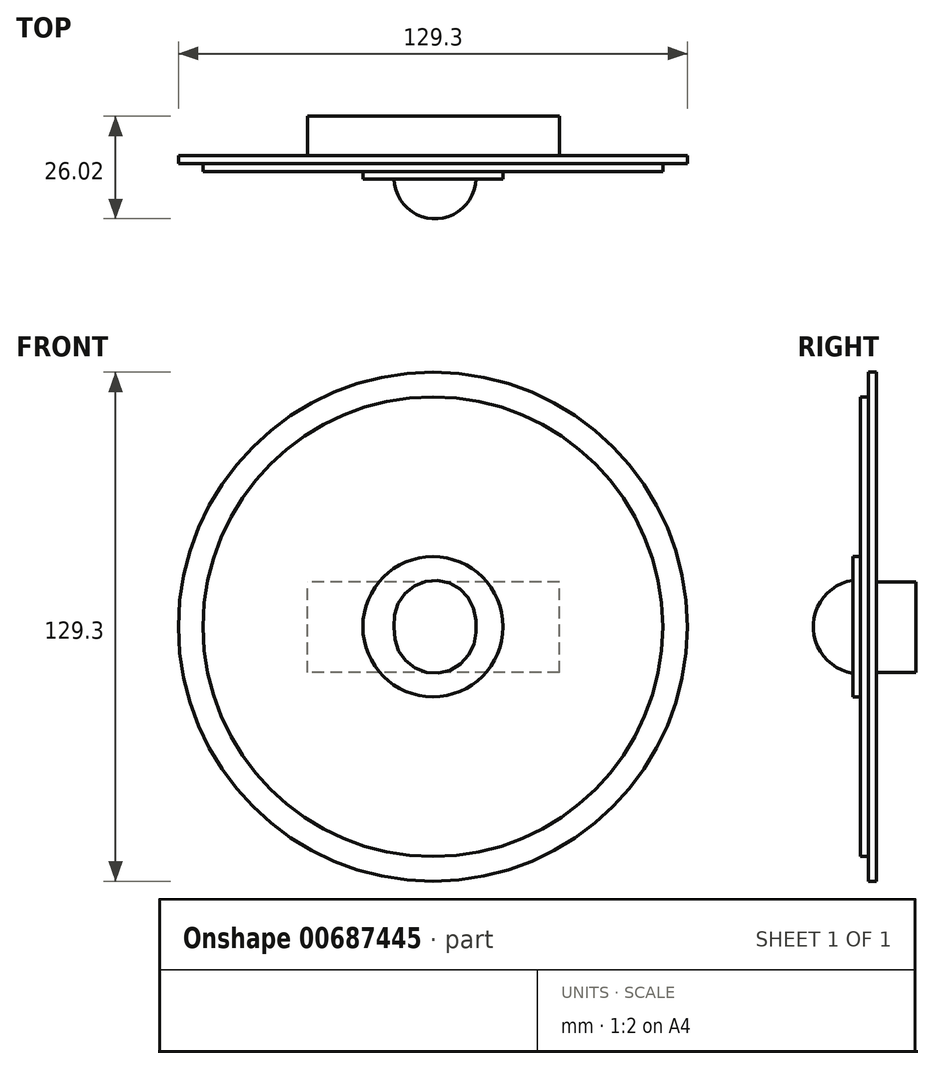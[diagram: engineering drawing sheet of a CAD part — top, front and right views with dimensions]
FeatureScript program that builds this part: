
annotation { "Feature Type Name" : "Feature", "Feature Type Description" : "" }
export const myFeature = defineFeature(function(context is Context, id is Id, definition is map)
    precondition{}
    {
        {
            var Q0;
            Q0=qCreatedBy(makeId("Front.planeOp"),FACE);
            var sketch = newSketch(context, id + "F0", { "sketchPlane" : qUnion([Q0])});
            skCircle(sketch, "E0", {"center": v(0, 0) * mm, "radius": 64.65 * mm});
            skSolve(sketch);
        }
        {
            var Q0;
            Q0 = qSketchRegion(id + "F0", true);
            extrude(context, id + "F1", {"entities" : qUnion([Q0]), "depth" : 2 * mm, "offsetDistance" : 25.4 * mm});
        }
        {
            var Q0;
            Q0=makeQuery(id+"F1.opExtrude","CAP_FACE",FACE,{"disambiguationData":[OSD([sQuery(id+"F0.wireOp",EDGE,"E0")])],"isStart":false});
            var sketch = newSketch(context, id + "F2", { "sketchPlane" : qUnion([Q0])});
            skCircle(sketch, "E1", {"center": v(0, 0) * mm, "radius": 58.4 * mm});
            skSolve(sketch);
        }
        {
            var Q0;
            Q0 = qSketchRegion(id + "F2", true);
            extrude(context, id + "F3", {"entities" : qUnion([Q0]), "operationType" : NewBodyOperationType.ADD, "depth" : 2 * mm, "offsetDistance" : 25.4 * mm});
        }
        {
            var Q0;
            Q0=qCreatedBy(makeId("Top.planeOp"),FACE);
            var sketch = newSketch(context, id + "F4", { "sketchPlane" : qUnion([Q0])});
            skArc(sketch, "E2", {"start": v(-9.82, -4.3) * mm, "mid": v(0.78, -16.02) * mm, "end": v(10.8, -3.8) * mm});
            skLineSegment(sketch, "E3", {"start": v(-9.82, -4.3) * mm, "end": v(10.8, -3.8) * mm});
            skSolve(sketch);
        }
        {
            var Q0;
            Q0 = qSketchRegion(id + "F4", true);
            var Q1;
            Q1=sQuery(id+"F4.wireOp",EDGE,"E3");
            revolve(context, id + "F5", {"operationType" : NewBodyOperationType.ADD, "entities" : qUnion([Q0]), "axis" : qUnion([Q1]), "revolveType" : RevolveType.FULL});
        }
        {
            var Q0;
            Q0=makeQuery(id+"F1.opExtrude","CAP_FACE",FACE,{"disambiguationData":[OSD([sQuery(id+"F0.wireOp",EDGE,"E0")])],"isStart":true});
            var sketch = newSketch(context, id + "F6", { "sketchPlane" : qUnion([Q0])});
            skLineSegment(sketch, "E4.bottom", {"start": v(-32.15, -11.66) * mm, "end": v(31.9, -11.66) * mm});
            skLineSegment(sketch, "E4.top", {"start": v(-32.15, 11.41) * mm, "end": v(31.9, 11.41) * mm});
            skLineSegment(sketch, "E4.left", {"start": v(-32.15, -11.66) * mm, "end": v(-32.15, 11.41) * mm});
            skLineSegment(sketch, "E4.right", {"start": v(31.9, -11.66) * mm, "end": v(31.9, 11.41) * mm});
            skSolve(sketch);
        }
        {
            var Q0;
            Q0 = qSketchRegion(id + "F6", true);
            extrude(context, id + "F7", {"entities" : qUnion([Q0]), "operationType" : NewBodyOperationType.ADD, "depth" : 10 * mm, "offsetDistance" : 25.4 * mm});
        }
        {
            var Q0;
            Q0=makeQuery(id+"F3.opExtrude","CAP_FACE",FACE,{"disambiguationData":[OSD([sQuery(id+"F2.wireOp",EDGE,"E1")])],"isStart":false});
            var sketch = newSketch(context, id + "F8", { "sketchPlane" : qUnion([Q0])});
            skCircle(sketch, "E5", {"center": v(0, 0) * mm, "radius": 17.8 * mm});
            skSolve(sketch);
        }
        {
            var Q0;
            Q0 = qSketchRegion(id + "F8", true);
            extrude(context, id + "F9", {"entities" : qUnion([Q0]), "operationType" : NewBodyOperationType.ADD, "depth" : 2 * mm, "offsetDistance" : 25.4 * mm});
        }
    });
